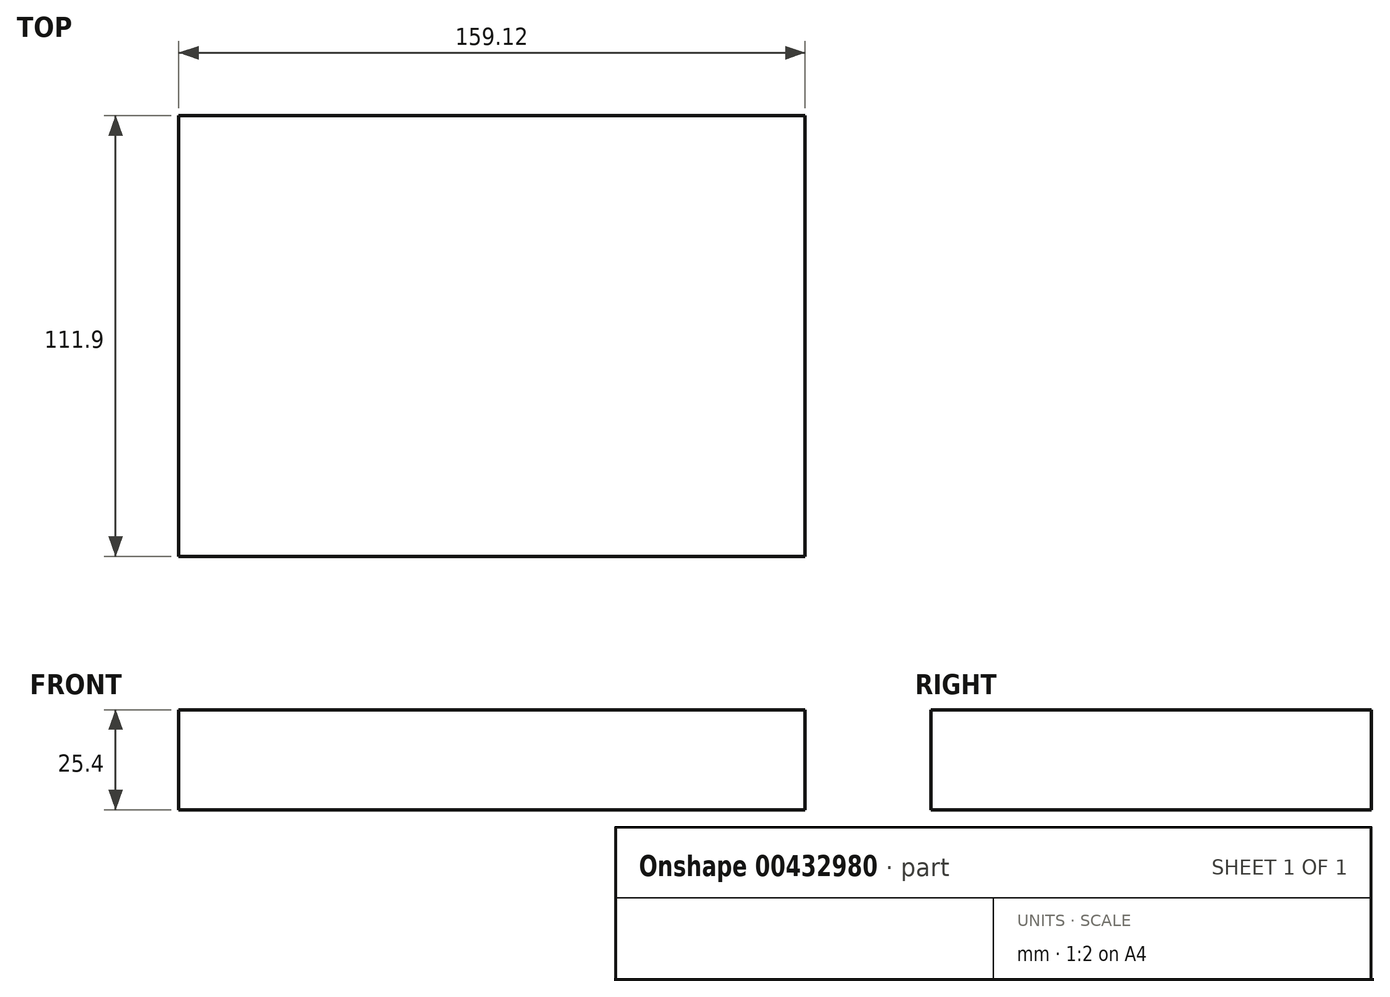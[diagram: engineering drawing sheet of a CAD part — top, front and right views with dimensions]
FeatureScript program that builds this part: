
annotation { "Feature Type Name" : "Feature", "Feature Type Description" : "" }
export const myFeature = defineFeature(function(context is Context, id is Id, definition is map)
    precondition{}
    {
        {
            var Q0;
            Q0=qCreatedBy(makeId("Top.planeOp"),FACE);
            var sketch = newSketch(context, id + "F0", { "sketchPlane" : qUnion([Q0])});
            skLineSegment(sketch, "E0.bottom", {"start": v(-79.56, 55.95) * mm, "end": v(79.56, 55.95) * mm});
            skLineSegment(sketch, "E0.top", {"start": v(-79.56, -55.95) * mm, "end": v(79.56, -55.95) * mm});
            skLineSegment(sketch, "E0.left", {"start": v(-79.56, 55.95) * mm, "end": v(-79.56, -55.95) * mm});
            skLineSegment(sketch, "E0.right", {"start": v(79.56, 55.95) * mm, "end": v(79.56, -55.95) * mm});
            skPoint(sketch, "E0.middle", {"position": v(0, 0) * mm});
            skSolve(sketch);
        }
        {
            var Q0;
            Q0=makeQuery(id+"F0.imprint","IMPRINT",FACE,{"disambiguationData":[TD([[makeQuery(id+"F0.imprint","IMPRINT",EDGE,{"derivedFrom":sQuery(id+"F0.wireOp",EDGE,"E0.bottom")}),-1.0]])]});
            extrude(context, id + "F1", {"entities" : qUnion([Q0]), "depth" : 25.4 * mm});
        }
    });
